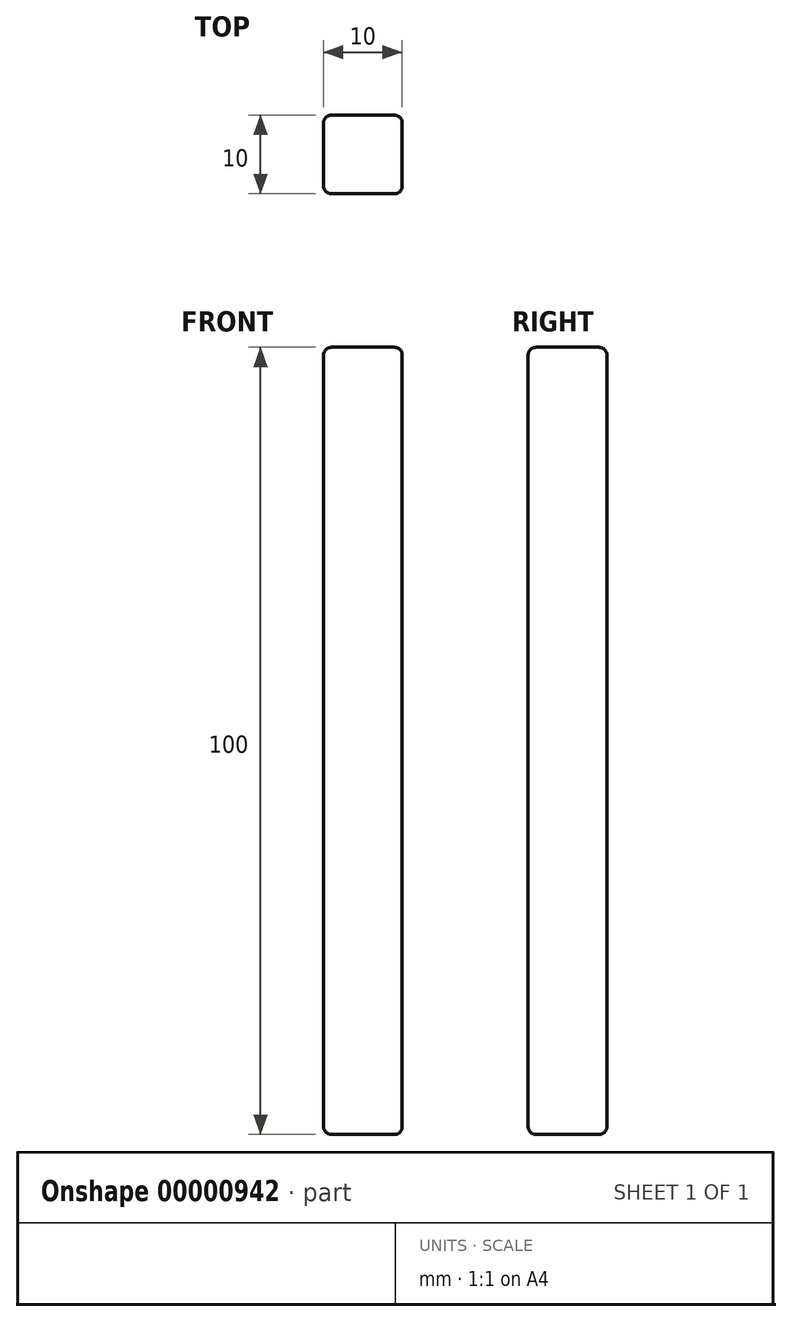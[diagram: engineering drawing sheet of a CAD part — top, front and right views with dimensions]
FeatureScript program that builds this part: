
annotation { "Feature Type Name" : "Feature", "Feature Type Description" : "" }
export const myFeature = defineFeature(function(context is Context, id is Id, definition is map)
    precondition{}
    {
        {
            var Q0;
            Q0=qCreatedBy(makeId("Front.planeOp"),FACE);
            var sketch = newSketch(context, id + "F0", { "sketchPlane" : qUnion([Q0])});
            skLineSegment(sketch, "E0.bottom", {"start": v(-37.98, -43.68) * mm, "end": v(-47.98, -43.68) * mm});
            skLineSegment(sketch, "E0.top", {"start": v(-37.98, 56.32) * mm, "end": v(-47.98, 56.32) * mm});
            skLineSegment(sketch, "E0.left", {"start": v(-37.98, -43.68) * mm, "end": v(-37.98, 56.32) * mm});
            skLineSegment(sketch, "E0.right", {"start": v(-47.98, -43.68) * mm, "end": v(-47.98, 56.32) * mm});
            skCircle(sketch, "E1", {"center": v(-42.98, 51.07) * mm, "radius": 7.25 * mm, "construction": true});
            skPoint(sketch, "E1.second.point", {"position": v(-47.98, 45.82) * mm});
            skLineSegment(sketch, "E2", {"start": v(-37.98, 6.32) * mm, "end": v(-47.98, 6.32) * mm, "construction": true});
            skCircle(sketch, "E3.0.MirrorC", {"center": v(-42.98, -38.43) * mm, "radius": 7.25 * mm, "construction": true});
            skSolve(sketch);
        }
        {
            var Q0;
            Q0=makeQuery(id+"F0.imprint","IMPRINT",FACE,{"disambiguationData":[TD([[makeQuery(id+"F0.imprint","IMPRINT",EDGE,{"derivedFrom":sQuery(id+"F0.wireOp",EDGE,"E0.bottom")}),-1.0]])]});
            extrude(context, id + "F1", {"entities" : qUnion([Q0]), "depth" : 10 * mm});
        }
        {
            var Q0;
            Q0=makeQuery(id+"F1.opExtrude","CAP_EDGE",EDGE,{"disambiguationData":[OSD([sQuery(id+"F0.wireOp",EDGE,"E0.right")])],"isStart":true});
            var Q1;
            Q1=makeQuery(id+"F1.opExtrude","CAP_EDGE",EDGE,{"disambiguationData":[OSD([sQuery(id+"F0.wireOp",EDGE,"E0.left")])],"isStart":true});
            var Q2;
            Q2=makeQuery(id+"F1.opExtrude","CAP_EDGE",EDGE,{"disambiguationData":[OSD([sQuery(id+"F0.wireOp",EDGE,"E0.right")])],"isStart":false});
            var Q3;
            Q3=makeQuery(id+"F1.opExtrude","CAP_EDGE",EDGE,{"disambiguationData":[OSD([sQuery(id+"F0.wireOp",EDGE,"E0.left")])],"isStart":false});
            var Q4;
            Q4=makeQuery(id+"F1.opExtrude","SWEPT_FACE",FACE,{"disambiguationData":[OSD([sQuery(id+"F0.wireOp",EDGE,"E0.top")])]});
            var Q5;
            Q5=makeQuery(id+"F1.opExtrude","SWEPT_FACE",FACE,{"disambiguationData":[OSD([sQuery(id+"F0.wireOp",EDGE,"E0.bottom")])]});
            fillet(context, id + "F2", {"entities" : qUnion([Q0, Q1, Q2, Q3, Q4, Q5]), "radius" : 1 * mm, "tangentPropagation" : true, "allowEdgeOverflow" : false});
        }
    });
